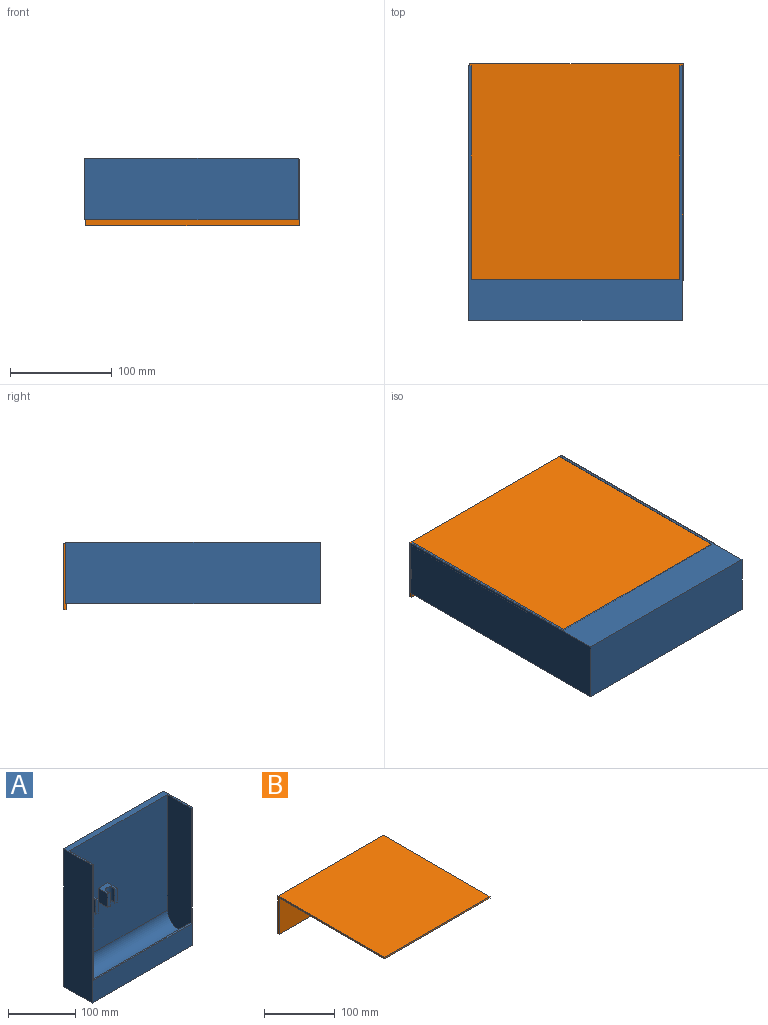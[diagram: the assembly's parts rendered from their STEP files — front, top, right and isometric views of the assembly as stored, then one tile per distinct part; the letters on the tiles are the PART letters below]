
ASSEMBLY  parts=2 mates=1
PART A: 25 faces, bbox 210x60x250 mm
  f0: plane 25x5.1mm, normal (0,-1,0), area 127.5mm2, adj f19,f20,f21,f24
  f1: plane 25x5.1mm, normal (0,-1,0), area 127.5mm2, adj f14,f15,f16,f23
  f2: plane 205x2.5mm, normal (0,0,1), area 512.5mm2, adj f4,f6,f11,f12
  f3: plane 210x205mm, normal (0,-1,0), area 42050mm2, adj f4,f7,f11,f12,f13,f14,f15,f16
  f4: cylinder r=23.75mm len=205mm, axis (-1,0,0), area 15295.6mm2, adj f2,f3,f11,f12
  f5: plane 250x60mm, normal (-1,0,0), area 15000mm2, adj f6,f7,f8,f10
  f6: plane 250x210mm, normal (0,-1,0), area 9450mm2, adj f2,f5,f7,f9,f10,f11,f12
  f7: plane 210x60mm, normal (0,0,1), area 2350mm2, adj f3,f5,f6,f8,f9,f11,f12
  f8: plane 250x210mm, normal (0,1,0), area 52500mm2, adj f5,f7,f9,f10
  f9: plane 250x60mm, normal (1,0,0), area 15000mm2, adj f6,f7,f8,f10
  f10: plane 210x60mm, normal (0,0,-1), area 12600mm2, adj f5,f6,f8,f9
  f11: plane 233.75x50mm, normal (-1,0,0), area 11386mm2, adj f2,f3,f4,f6,f7
  f12: plane 233.75x50mm, normal (1,0,0), area 11386mm2, adj f2,f3,f4,f6,f7
  f13: plane 25x20mm, normal (-1,0,0), area 500mm2, adj f3,f14,f16,f17
  f14: plane 20x20mm, normal (0,0,-1), area 259.6mm2, adj f1,f3,f13,f15,f17,f23
  f15: plane 25x20mm, normal (1,0,0), area 500mm2, adj f1,f3,f14,f16
  f16: plane 20x20mm, normal (0,0,1), area 259.6mm2, adj f1,f3,f13,f15,f17,f23
  f17: plane 25x5.1mm, normal (0,-1,0), area 127.5mm2, adj f13,f14,f16,f23
  f18: plane 25x20mm, normal (-1,0,0), area 500mm2, adj f3,f19,f21,f22
  f19: plane 20x20mm, normal (0,0,-1), area 259.6mm2, adj f0,f3,f18,f20,f22,f24
  f20: plane 25x20mm, normal (1,0,0), area 500mm2, adj f0,f3,f19,f21
  f21: plane 20x20mm, normal (0,0,1), area 259.6mm2, adj f0,f3,f18,f20,f22,f24
  f22: plane 25x5.1mm, normal (0,-1,0), area 127.5mm2, adj f18,f19,f21,f24
  f23: cylinder r=7mm len=25mm, axis (0,0,1), area 828.2mm2, adj f1,f14,f16,f17
  f24: cylinder r=7mm len=25mm, axis (0,0,1), area 828.2mm2, adj f0,f19,f21,f22
PART B: 8 faces, bbox 210x212.5x65 mm
  f0: plane 210x210mm, normal (0,0,-1), area 44100mm2, adj f1,f2,f3,f6
  f1: plane 212.5x65mm, normal (-1,0,0), area 687.5mm2, adj f0,f2,f4,f5,f6,f7
  f2: plane 210x2.5mm, normal (0,-1,0), area 525mm2, adj f0,f1,f3,f4
  f3: plane 212.5x65mm, normal (1,0,0), area 687.5mm2, adj f0,f2,f4,f5,f6,f7
  f4: plane 212.5x210mm, normal (0,0,1), area 44625mm2, adj f1,f2,f3,f5
  f5: plane 210x65mm, normal (0,1,0), area 13650mm2, adj f1,f3,f4,f7
  f6: plane 210x62.5mm, normal (0,-1,0), area 13125mm2, adj f0,f1,f3,f7
  f7: plane 210x2.5mm, normal (0,0,-1), area 525mm2, adj f1,f3,f5,f6
PLACE A rot(axis=(-1,0,0),90deg) t=(-208.36,4.35,59.84)mm
PLACE B t=(13.78,171.46,81.27)mm
MATE parallel B.f6 <-> A.f7  axis (0,-1,0) through (-122.26,253.81,50.02)mm
